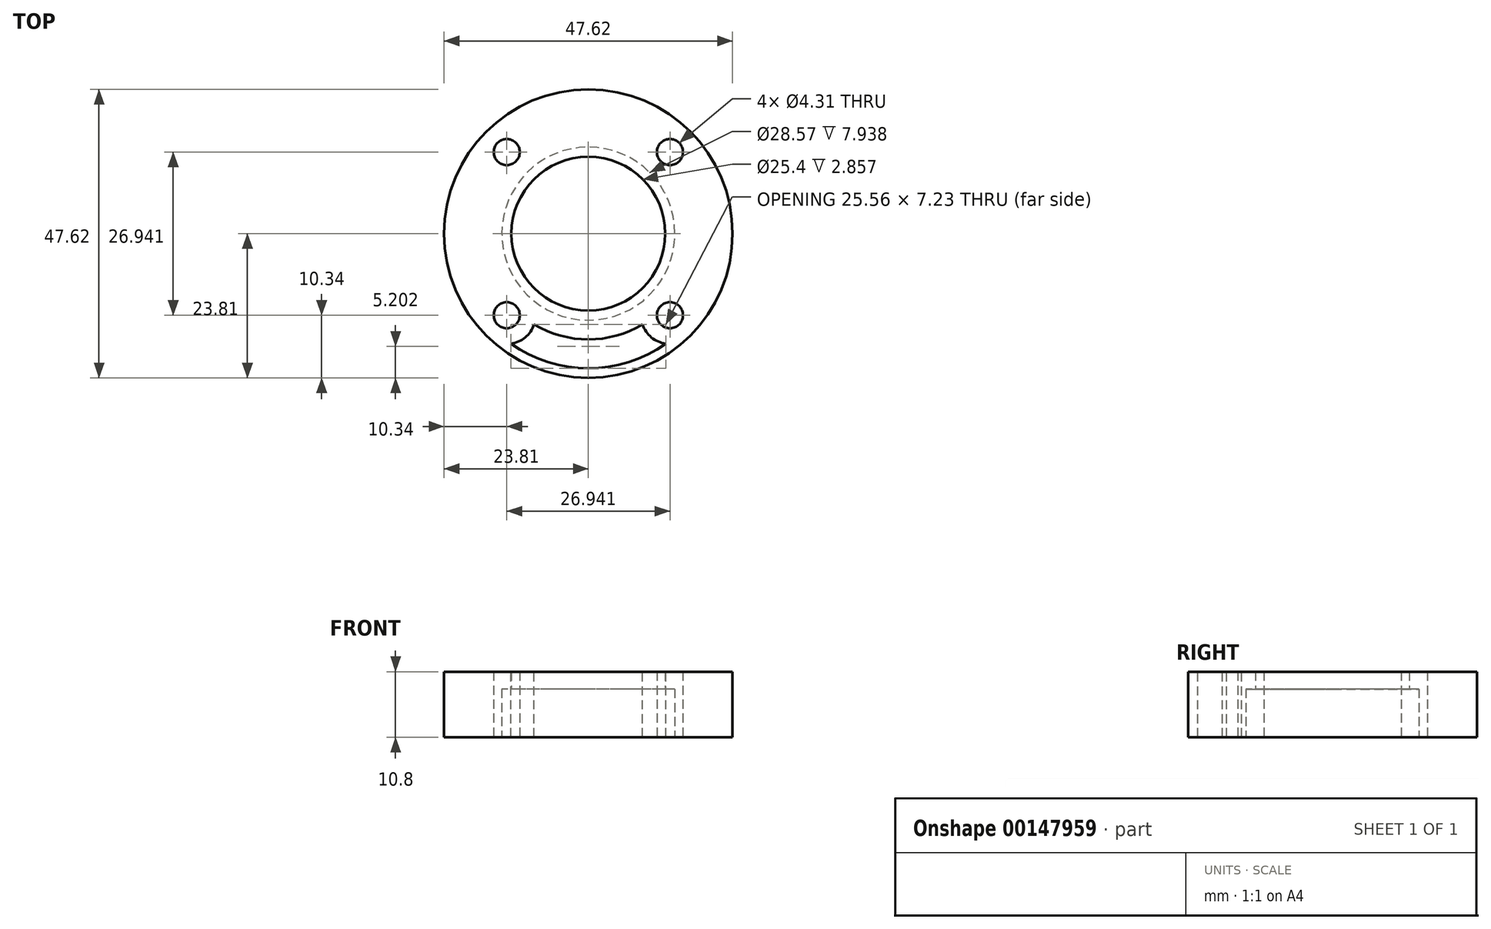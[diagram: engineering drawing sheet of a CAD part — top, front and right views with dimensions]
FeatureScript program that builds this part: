
annotation { "Feature Type Name" : "Feature", "Feature Type Description" : "" }
export const myFeature = defineFeature(function(context is Context, id is Id, definition is map)
    precondition{}
    {
        {
            var Q0;
            Q0=qCreatedBy(makeId("Top.planeOp"),FACE);
            var sketch = newSketch(context, id + "F0", { "sketchPlane" : qUnion([Q0])});
            skCircle(sketch, "E0", {"center": v(0, 0) * mm, "radius": 14.29 * mm});
            skCircle(sketch, "E1", {"center": v(0, 0) * mm, "radius": 23.81 * mm});
            skCircle(sketch, "E2", {"center": v(13.47, 13.47) * mm, "radius": 4.76 * mm, "construction": true});
            skCircle(sketch, "E3", {"center": v(13.47, 13.47) * mm, "radius": 2.15 * mm});
            skCircle(sketch, "E4", {"center": v(13.47, -13.47) * mm, "radius": 2.15 * mm});
            skCircle(sketch, "E5", {"center": v(-13.47, -13.47) * mm, "radius": 2.15 * mm});
            skLineSegment(sketch, "E6.bottom", {"start": v(13.47, 13.47) * mm, "end": v(-13.47, 13.47) * mm, "construction": true});
            skLineSegment(sketch, "E6.top", {"start": v(13.47, -13.47) * mm, "end": v(-13.47, -13.47) * mm, "construction": true});
            skLineSegment(sketch, "E6.left", {"start": v(13.47, 13.47) * mm, "end": v(13.47, -13.47) * mm, "construction": true});
            skLineSegment(sketch, "E6.right", {"start": v(-13.47, 13.47) * mm, "end": v(-13.47, -13.47) * mm, "construction": true});
            skCircle(sketch, "E7", {"center": v(-13.47, 13.47) * mm, "radius": 2.15 * mm});
            skSolve(sketch);
        }
        {
            var Q0;
            Q0=makeQuery(id+"F0.imprint","IMPRINT",FACE,{"disambiguationData":[TD([[makeQuery(id+"F0.imprint","IMPRINT",EDGE,{"derivedFrom":sQuery(id+"F0.wireOp",EDGE,"E0")}),-1.0]])]});
            extrude(context, id + "F1", {"entities" : qUnion([Q0]), "depth" : 7.94 * mm});
        }
        {
            var Q0;
            Q0=makeQuery(id+"F1.opExtrude","CAP_FACE",FACE,{"disambiguationData":[OSD([sQuery(id+"F0.wireOp",EDGE,"E0"),sQuery(id+"F0.wireOp",EDGE,"E1"),sQuery(id+"F0.wireOp",EDGE,"E3"),sQuery(id+"F0.wireOp",EDGE,"E4"),sQuery(id+"F0.wireOp",EDGE,"E5")])],"isStart":false});
            var sketch = newSketch(context, id + "F2", { "sketchPlane" : qUnion([Q0])});
            skArc(sketch, "E8", {"start": v(8.96, -15) * mm, "mid": v(10.42, -17.13) * mm, "end": v(12.78, -18.18) * mm});
            skArc(sketch, "E9", {"start": v(-12.78, -18.18) * mm, "mid": v(-10.42, -17.13) * mm, "end": v(-8.96, -15) * mm});
            skArc(sketch, "E10", {"start": v(-12.78, -18.18) * mm, "mid": v(0, -22.23) * mm, "end": v(12.78, -18.18) * mm});
            skArc(sketch, "E11", {"start": v(-8.96, -15) * mm, "mid": v(0, -17.46) * mm, "end": v(8.96, -15) * mm});
            skSolve(sketch);
        }
        {
            var Q0;
            Q0=qSketchRegion(id+"F2",true);
            var Q1;
            Q1=makeQuery(id+"F1.opExtrude","CAP_FACE",FACE,{"disambiguationData":[OSD([sQuery(id+"F0.wireOp",EDGE,"E0"),sQuery(id+"F0.wireOp",EDGE,"E1"),sQuery(id+"F0.wireOp",EDGE,"E3"),sQuery(id+"F0.wireOp",EDGE,"E4"),sQuery(id+"F0.wireOp",EDGE,"E5")])],"isStart":true});
            extrude(context, id + "F3", {"entities" : qUnion([Q0]), "operationType" : NewBodyOperationType.REMOVE, "endBound" : BoundingType.UP_TO_SURFACE, "oppositeDirection" : true, "endBoundEntityFace" : qUnion([Q1]), "depth" : 25.4 * mm});
        }
        {
            var Q0;
            Q0=makeQuery(id+"F1.opExtrude","CAP_FACE",FACE,{"disambiguationData":[OSD([sQuery(id+"F0.wireOp",EDGE,"E0"),sQuery(id+"F0.wireOp",EDGE,"E1"),sQuery(id+"F0.wireOp",EDGE,"E3"),sQuery(id+"F0.wireOp",EDGE,"E4"),sQuery(id+"F0.wireOp",EDGE,"E5")])],"isStart":false});
            var sketch = newSketch(context, id + "F4", { "sketchPlane" : qUnion([Q0])});
            skCircle(sketch, "E12", {"center": v(0, 0) * mm, "radius": 23.81 * mm});
            skCircle(sketch, "E13", {"center": v(0, 0) * mm, "radius": 12.7 * mm});
            skCircle(sketch, "E14", {"center": v(-13.47, -13.47) * mm, "radius": 2.15 * mm});
            skCircle(sketch, "E15", {"center": v(13.47, 13.47) * mm, "radius": 2.15 * mm});
            skCircle(sketch, "E16", {"center": v(13.47, -13.47) * mm, "radius": 2.15 * mm});
            skCircle(sketch, "E17", {"center": v(-13.47, 13.47) * mm, "radius": 2.15 * mm});
            skSolve(sketch);
        }
        {
            var Q0;
            Q0=makeQuery(id+"F4.imprint","IMPRINT",FACE,{"disambiguationData":[TD([[makeQuery(id+"F4.imprint","IMPRINT",EDGE,{"derivedFrom":sQuery(id+"F4.wireOp",EDGE,"E12")}),1.0]])]});
            var Q1;
            Q1=makeQuery(id+"F4.imprint","IMPRINT",FACE,{"disambiguationData":[TD([[makeQuery(id+"F4.imprint","IMPRINT",EDGE,{"derivedFrom":sQuery(id+"F4.wireOp",EDGE,"E13")}),-1.0]])]});
            var Q2;
            Q2=makeQuery(id+"F4.imprint","IMPRINT",FACE,{"disambiguationData":[TD([[makeQuery(id+"F4.imprint","IMPRINT",EDGE,{"derivedFrom":makeQuery(id+"FNOmxEsCR3imQyS_1.2.F3.boolean.opBoolean","COPY",EDGE,{"derivedFrom":makeQuery(id+"FNOmxEsCR3imQyS_1.2.F3.opExtrude","CAP_EDGE",EDGE,{"disambiguationData":[OSD([sQuery(id+"F2.wireOp",EDGE,"E8")])],"isStart":true})})}),-1.0]])]});
            var Q3;
            Q3=makeQuery(id+"F4.imprint","IMPRINT",FACE,{"disambiguationData":[TD([[makeQuery(id+"F4.imprint","IMPRINT",EDGE,{"derivedFrom":makeQuery(id+"FNOmxEsCR3imQyS_1.1.F3.boolean.opBoolean","COPY",EDGE,{"derivedFrom":makeQuery(id+"FNOmxEsCR3imQyS_1.1.F3.opExtrude","CAP_EDGE",EDGE,{"disambiguationData":[OSD([sQuery(id+"F2.wireOp",EDGE,"E8")])],"isStart":true})})}),-1.0]])]});
            var Q4;
            Q4=makeQuery(id+"F4.imprint","IMPRINT",FACE,{"disambiguationData":[TD([[makeQuery(id+"F4.imprint","IMPRINT",EDGE,{"derivedFrom":makeQuery(id+"F3.boolean.opBoolean","COPY",EDGE,{"derivedFrom":makeQuery(id+"F3.opExtrude","CAP_EDGE",EDGE,{"disambiguationData":[OSD([sQuery(id+"F2.wireOp",EDGE,"E8")])],"isStart":true})})}),-1.0]])]});
            var Q5;
            Q5=makeQuery(id+"F4.imprint","IMPRINT",FACE,{"disambiguationData":[TD([[makeQuery(id+"F4.imprint","IMPRINT",EDGE,{"derivedFrom":makeQuery(id+"FNOmxEsCR3imQyS_1.3.F3.boolean.opBoolean","COPY",EDGE,{"derivedFrom":makeQuery(id+"FNOmxEsCR3imQyS_1.3.F3.opExtrude","CAP_EDGE",EDGE,{"disambiguationData":[OSD([sQuery(id+"F2.wireOp",EDGE,"E8")])],"isStart":true})})}),-1.0]])]});
            extrude(context, id + "F5", {"entities" : qUnion([Q0, Q1, Q2, Q3, Q4, Q5]), "operationType" : NewBodyOperationType.ADD, "depth" : 2.86 * mm});
        }
    });
